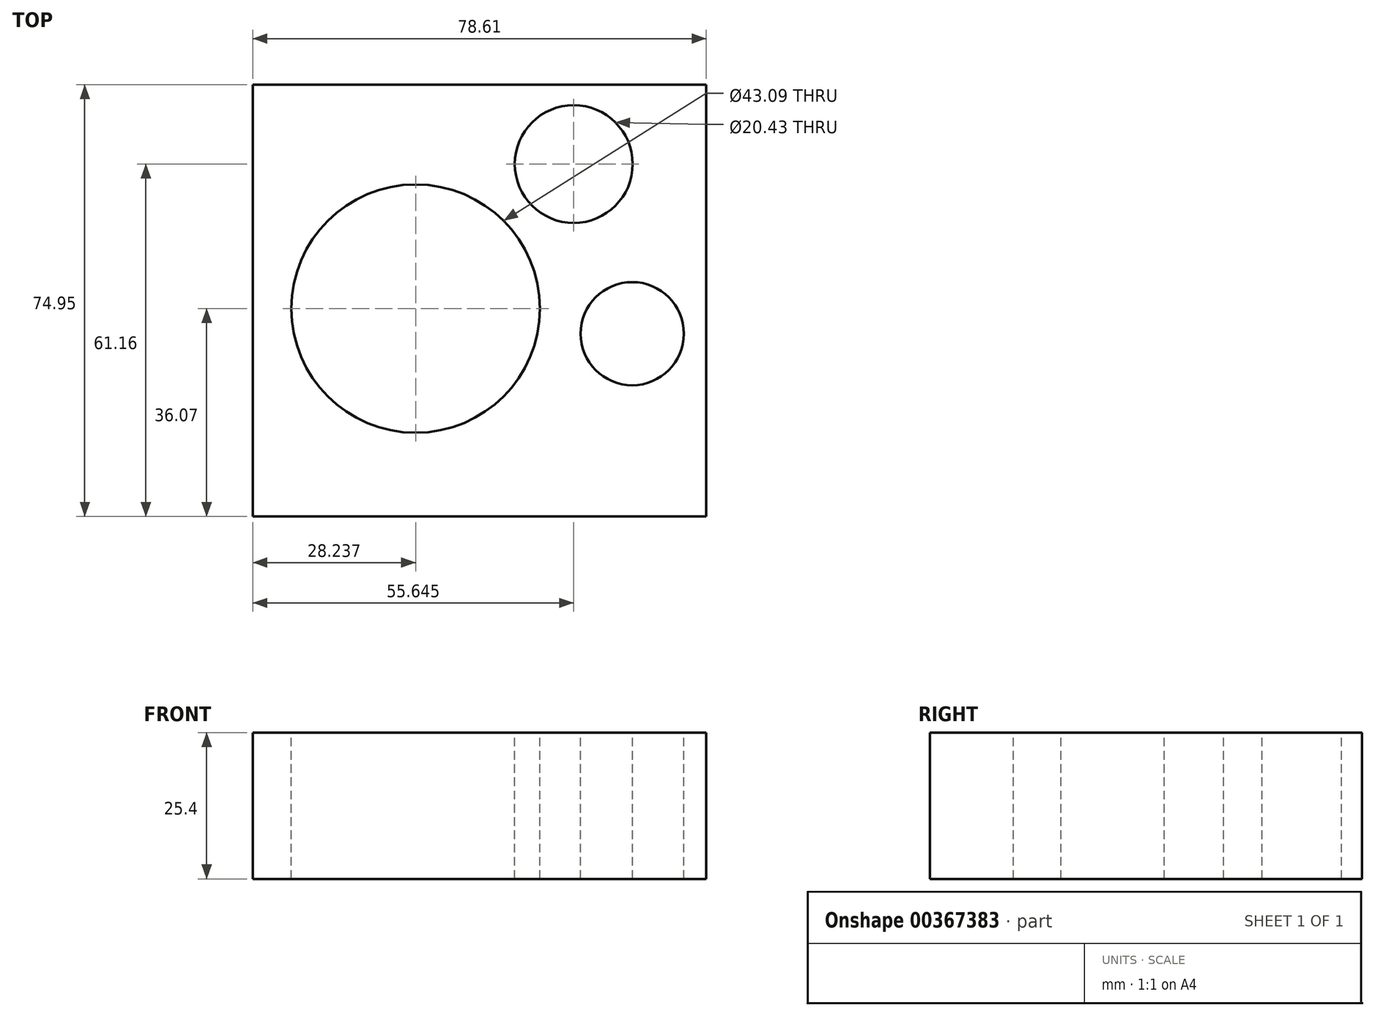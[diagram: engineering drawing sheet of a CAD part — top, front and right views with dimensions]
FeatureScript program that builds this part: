
annotation { "Feature Type Name" : "Feature", "Feature Type Description" : "" }
export const myFeature = defineFeature(function(context is Context, id is Id, definition is map)
    precondition{}
    {
        {
            var Q0;
            Q0=qCreatedBy(makeId("Top.planeOp"),FACE);
            var sketch = newSketch(context, id + "F0", { "sketchPlane" : qUnion([Q0])});
            skLineSegment(sketch, "E0.bottom", {"start": v(-34.24, 43.23) * mm, "end": v(44.37, 43.23) * mm});
            skLineSegment(sketch, "E0.top", {"start": v(-34.24, -31.72) * mm, "end": v(44.37, -31.72) * mm});
            skLineSegment(sketch, "E0.left", {"start": v(-34.24, 43.23) * mm, "end": v(-34.24, -31.72) * mm});
            skLineSegment(sketch, "E0.right", {"start": v(44.37, 43.23) * mm, "end": v(44.37, -31.72) * mm});
            skSolve(sketch);
        }
        {
            var Q0;
            Q0 = qSketchRegion(id + "F0", true);
            extrude(context, id + "F1", {"entities" : qUnion([Q0]), "depth" : 25.4 * mm});
        }
        {
            var Q0;
            Q0=makeQuery(id+"F1.opExtrude","CAP_FACE",FACE,{"disambiguationData":[OSD([sQuery(id+"F0.wireOp",EDGE,"E0.bottom"),sQuery(id+"F0.wireOp",EDGE,"E0.top"),sQuery(id+"F0.wireOp",EDGE,"E0.left"),sQuery(id+"F0.wireOp",EDGE,"E0.right")])],"isStart":false});
            var sketch = newSketch(context, id + "F2", { "sketchPlane" : qUnion([Q0])});
            skCircle(sketch, "E1", {"center": v(-6, 4.35) * mm, "radius": 21.55 * mm});
            skCircle(sketch, "E2", {"center": v(21.4, 29.44) * mm, "radius": 10.22 * mm});
            skCircle(sketch, "E3", {"center": v(31.55, 0) * mm, "radius": 8.95 * mm});
            skSolve(sketch);
        }
        {
            var Q0;
            Q0 = qSketchRegion(id + "F2", true);
            var Q1;
            Q1=makeQuery(id+"F1.opExtrude","CAP_FACE",FACE,{"disambiguationData":[OSD([sQuery(id+"F0.wireOp",EDGE,"E0.bottom"),sQuery(id+"F0.wireOp",EDGE,"E0.top"),sQuery(id+"F0.wireOp",EDGE,"E0.left"),sQuery(id+"F0.wireOp",EDGE,"E0.right")])],"isStart":true});
            extrude(context, id + "F3", {"entities" : qUnion([Q0]), "operationType" : NewBodyOperationType.REMOVE, "endBound" : BoundingType.UP_TO_SURFACE, "oppositeDirection" : true, "endBoundEntityFace" : qUnion([Q1]), "depth" : 25.4 * mm});
        }
    });
